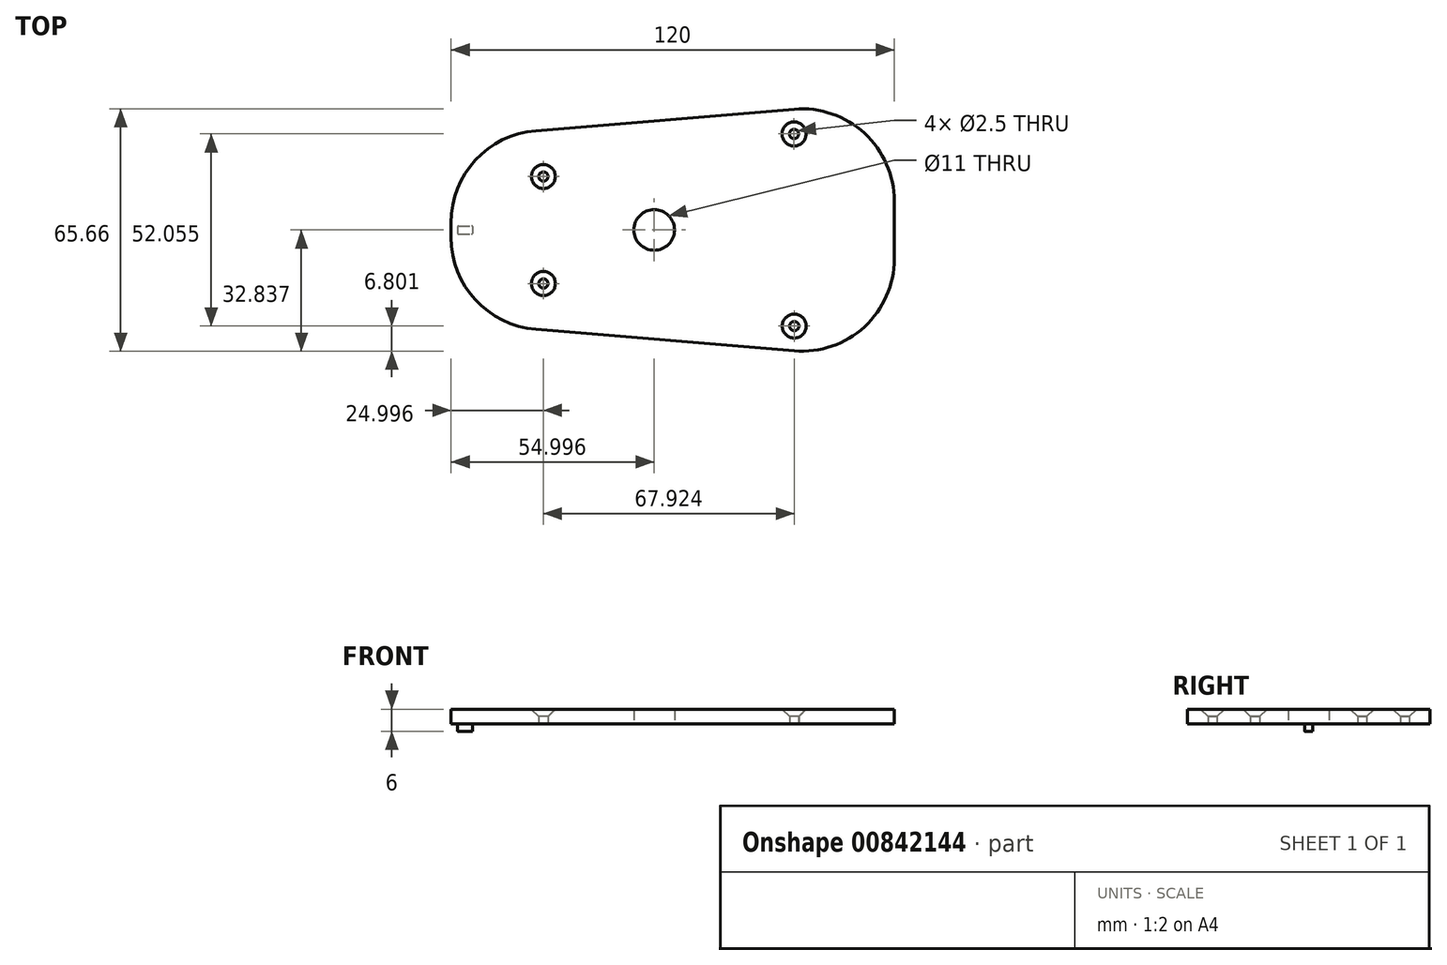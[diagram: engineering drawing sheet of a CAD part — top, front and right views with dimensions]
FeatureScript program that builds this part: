
annotation { "Feature Type Name" : "Feature", "Feature Type Description" : "" }
export const myFeature = defineFeature(function(context is Context, id is Id, definition is map)
    precondition{}
    {
        {
            var Q0;
            Q0=qCreatedBy(makeId("Top.planeOp"),FACE);
            var sketch = newSketch(context, id + "F0", { "sketchPlane" : qUnion([Q0])});
            skArc(sketch, "E0.0.0", {"start": v(-46.03, 5.44) * mm, "mid": v(-48.71, 1) * mm, "end": v(-53.63, -0.65) * mm});
            skLineSegment(sketch, "E0.0.1", {"start": v(-53.63, -0.65) * mm, "end": v(-59.43, -0.65) * mm});
            skLineSegment(sketch, "E0.0.2", {"start": v(-59.43, -0.65) * mm, "end": v(-59.43, -1.35) * mm});
            skArc(sketch, "E0.0.3", {"start": v(-59.43, -1.35) * mm, "mid": v(-52.83, -18.28) * mm, "end": v(-36.5, -26.26) * mm});
            skLineSegment(sketch, "E0.0.4", {"start": v(-36.5, -26.26) * mm, "end": v(33.5, -32.1) * mm});
            skArc(sketch, "E0.0.5", {"start": v(33.5, -32.1) * mm, "mid": v(52.5, -25.58) * mm, "end": v(60.57, -7.18) * mm});
            skLineSegment(sketch, "E0.0.6", {"start": v(60.57, -7.18) * mm, "end": v(60.57, 8.48) * mm});
            skArc(sketch, "E0.0.7", {"start": v(60.57, 8.48) * mm, "mid": v(52.5, 26.88) * mm, "end": v(33.5, 33.4) * mm});
            skLineSegment(sketch, "E0.0.8", {"start": v(33.5, 33.4) * mm, "end": v(-36.5, 27.56) * mm});
            skArc(sketch, "E0.0.9", {"start": v(-36.5, 27.56) * mm, "mid": v(-52.83, 19.57) * mm, "end": v(-59.43, 2.64) * mm});
            skLineSegment(sketch, "E0.0.10", {"start": v(-59.43, 2.64) * mm, "end": v(-59.43, 1.95) * mm});
            skLineSegment(sketch, "E0.0.11", {"start": v(-59.43, 1.95) * mm, "end": v(-53.63, 1.95) * mm});
            skArc(sketch, "E0.0.12", {"start": v(-53.63, 1.95) * mm, "mid": v(-50.35, 2.85) * mm, "end": v(-48.4, 5.63) * mm});
            skArc(sketch, "E0.0.13", {"start": v(-48.4, 5.63) * mm, "mid": v(-40.83, 12.6) * mm, "end": v(-33.43, 5.44) * mm});
            skArc(sketch, "E0.0.14", {"start": v(-33.43, 5.44) * mm, "mid": v(-31.53, 2.84) * mm, "end": v(-28.43, 1.95) * mm});
            skLineSegment(sketch, "E0.0.15", {"start": v(-28.43, 1.95) * mm, "end": v(-15.43, 1.95) * mm});
            skLineSegment(sketch, "E0.0.16", {"start": v(-15.43, 1.95) * mm, "end": v(-15.43, 15.25) * mm});
            skLineSegment(sketch, "E0.0.17", {"start": v(-15.43, 15.25) * mm, "end": v(-4.93, 15.25) * mm});
            skLineSegment(sketch, "E0.0.18", {"start": v(-4.93, 15.25) * mm, "end": v(-4.93, 17.18) * mm});
            skArc(sketch, "E0.0.19", {"start": v(-4.93, 17.18) * mm, "mid": v(-0.83, 21.28) * mm, "end": v(3.27, 17.18) * mm});
            skLineSegment(sketch, "E0.0.20", {"start": v(3.27, 17.18) * mm, "end": v(3.27, 15.25) * mm});
            skLineSegment(sketch, "E0.0.21", {"start": v(3.27, 15.25) * mm, "end": v(29.22, 15.25) * mm});
            skLineSegment(sketch, "E0.0.22", {"start": v(29.22, 15.25) * mm, "end": v(29.22, 17.18) * mm});
            skArc(sketch, "E0.0.23", {"start": v(29.22, 17.18) * mm, "mid": v(33.32, 21.28) * mm, "end": v(37.42, 17.18) * mm});
            skLineSegment(sketch, "E0.0.24", {"start": v(37.42, 17.18) * mm, "end": v(37.42, 15.25) * mm});
            skLineSegment(sketch, "E0.0.25", {"start": v(37.42, 15.25) * mm, "end": v(47.92, 15.25) * mm});
            skLineSegment(sketch, "E0.0.26", {"start": v(47.92, 15.25) * mm, "end": v(47.92, -13.95) * mm});
            skLineSegment(sketch, "E0.0.27", {"start": v(47.92, -13.95) * mm, "end": v(37.42, -13.95) * mm});
            skLineSegment(sketch, "E0.0.28", {"start": v(37.42, -13.95) * mm, "end": v(37.42, -15.88) * mm});
            skArc(sketch, "E0.0.29", {"start": v(37.42, -15.88) * mm, "mid": v(33.32, -19.98) * mm, "end": v(29.22, -15.88) * mm});
            skLineSegment(sketch, "E0.0.30", {"start": v(29.22, -15.88) * mm, "end": v(29.22, -13.95) * mm});
            skLineSegment(sketch, "E0.0.31", {"start": v(29.22, -13.95) * mm, "end": v(3.27, -13.95) * mm});
            skLineSegment(sketch, "E0.0.32", {"start": v(3.27, -13.95) * mm, "end": v(3.27, -15.88) * mm});
            skArc(sketch, "E0.0.33", {"start": v(3.27, -15.88) * mm, "mid": v(-0.83, -19.98) * mm, "end": v(-4.93, -15.88) * mm});
            skLineSegment(sketch, "E0.0.34", {"start": v(-4.93, -15.88) * mm, "end": v(-4.93, -13.95) * mm});
            skLineSegment(sketch, "E0.0.35", {"start": v(-4.93, -13.95) * mm, "end": v(-15.43, -13.95) * mm});
            skLineSegment(sketch, "E0.0.36", {"start": v(-15.43, -13.95) * mm, "end": v(-15.43, -0.65) * mm});
            skLineSegment(sketch, "E0.0.37", {"start": v(-15.43, -0.65) * mm, "end": v(-28.43, -0.65) * mm});
            skArc(sketch, "E0.0.38", {"start": v(-28.43, -0.65) * mm, "mid": v(-33.36, 1) * mm, "end": v(-36.03, 5.44) * mm});
            skArc(sketch, "E0.0.39", {"start": v(-36.03, 5.44) * mm, "mid": v(-41.03, 10.44) * mm, "end": v(-46.03, 5.44) * mm});
            skCircle(sketch, "E1.0", {"center": v(-34.43, 15.14) * mm, "radius": 1.25 * mm});
            skPoint(sketch, "E2.0", {"position": v(-34.43, -13.85) * mm});
            skCircle(sketch, "E3.0", {"center": v(-34.43, -13.85) * mm, "radius": 1.25 * mm});
            skCircle(sketch, "E4.0", {"center": v(33.5, -25.38) * mm, "radius": 1.25 * mm});
            skCircle(sketch, "E5.0", {"center": v(33.43, 26.68) * mm, "radius": 1.25 * mm});
            skCircle(sketch, "E6", {"center": v(-4.43, 0.66) * mm, "radius": 5.5 * mm});
            skLineSegment(sketch, "E7", {"start": v(-53.63, 1.95) * mm, "end": v(-53.63, -0.65) * mm});
            skLineSegment(sketch, "E8", {"start": v(-57.63, 0.65) * mm, "end": v(-57.63, -0.65) * mm});
            skLineSegment(sketch, "E9", {"start": v(-57.63, -0.65) * mm, "end": v(-57.63, 1.95) * mm});
            skLineSegment(sketch, "E10", {"start": v(-59.43, 1.95) * mm, "end": v(-59.43, -0.65) * mm});
            skSolve(sketch);
        }
        {
            var Q0;
            Q0=makeQuery(id+"F0.imprint","IMPRINT",FACE,{"disambiguationData":[TD([[makeQuery(id+"F0.imprint","IMPRINT",EDGE,{"derivedFrom":sQuery(id+"F0.wireOp",EDGE,"f2d0978f-a5e2-4eee-89b1-d31b48b31204.0.0")}),1.0]])]});
            var Q1;
            Q1=makeQuery(id+"F0.imprint","IMPRINT",FACE,{"disambiguationData":[TD([[makeQuery(id+"F0.imprint","IMPRINT",EDGE,{"derivedFrom":sQuery(id+"F0.wireOp",EDGE,"ac3f7785-ddd1-404e-9a58-e7037b63adee.0")}),-1.0]])]});
            var Q2;
            {var subQ9=sQuery(id+"F0.wireOp",EDGE,"E0.0.0");Q2=makeQuery(id+"F0.imprint","IMPRINT",FACE,{"disambiguationData":[TD([[makeQuery(id+"F0.imprint","IMPRINT",EDGE,{"derivedFrom":subQ9}),1.0]])]});}
            var Q3;
            Q3=makeQuery(id+"F0.imprint","IMPRINT",FACE,{"disambiguationData":[TD([[makeQuery(id+"F0.imprint","IMPRINT",EDGE,{"derivedFrom":sQuery(id+"F0.wireOp",EDGE,"E0.0.0")}),-1.0]])]});
            var Q4;
            {var subQ6=sQuery(id+"F0.wireOp",EDGE,"E10");Q4=makeQuery(id+"F0.imprint","IMPRINT",FACE,{"disambiguationData":[TD([[makeQuery(id+"F0.imprint","IMPRINT",EDGE,{"derivedFrom":subQ6}),1.0]])]});}
            var Q5;
            {var subQ0=sQuery(id+"F0.wireOp",EDGE,"E7");Q5=makeQuery(id+"F0.imprint","IMPRINT",FACE,{"disambiguationData":[TD([[makeQuery(id+"F0.imprint","IMPRINT",EDGE,{"derivedFrom":subQ0}),-1.0]])]});}
            extrude(context, id + "F1", {"entities" : qUnion([Q0, Q1, Q2, Q3, Q4, Q5]), "depth" : 4 * mm, "offsetDistance" : 25 * mm});
        }
        {
            var Q0;
            Q0=makeQuery(id+"F1.opExtrude","CAP_FACE",FACE,{"disambiguationData":[OSD([sQuery(id+"F0.wireOp",EDGE,"E0.0.2"),sQuery(id+"F0.wireOp",EDGE,"E0.0.3"),sQuery(id+"F0.wireOp",EDGE,"E0.0.4"),sQuery(id+"F0.wireOp",EDGE,"E0.0.5"),sQuery(id+"F0.wireOp",EDGE,"E0.0.6"),sQuery(id+"F0.wireOp",EDGE,"E0.0.7"),sQuery(id+"F0.wireOp",EDGE,"E0.0.8"),sQuery(id+"F0.wireOp",EDGE,"E0.0.9"),sQuery(id+"F0.wireOp",EDGE,"E0.0.10"),sQuery(id+"F0.wireOp",EDGE,"E1.0"),sQuery(id+"F0.wireOp",EDGE,"E3.0"),sQuery(id+"F0.wireOp",EDGE,"E4.0"),sQuery(id+"F0.wireOp",EDGE,"E5.0"),sQuery(id+"F0.wireOp",EDGE,"E6"),sQuery(id+"F0.wireOp",EDGE,"E10")])],"isStart":true});
            var sketch = newSketch(context, id + "F2", { "sketchPlane" : qUnion([Q0])});
            skArc(sketch, "E11.0", {"start": v(-46.03, -5.44) * mm, "mid": v(-48.71, -1) * mm, "end": v(-53.63, 0.65) * mm});
            skLineSegment(sketch, "E11.1", {"start": v(-53.63, 0.65) * mm, "end": v(-59.43, 0.65) * mm});
            skLineSegment(sketch, "E11.2", {"start": v(-59.43, 0.65) * mm, "end": v(-59.43, 1.35) * mm});
            skArc(sketch, "E11.3", {"start": v(-59.43, 1.35) * mm, "mid": v(-52.83, 18.28) * mm, "end": v(-36.5, 26.26) * mm});
            skLineSegment(sketch, "E11.4", {"start": v(-36.5, 26.26) * mm, "end": v(33.5, 32.1) * mm});
            skArc(sketch, "E11.5", {"start": v(33.5, 32.1) * mm, "mid": v(52.5, 25.58) * mm, "end": v(60.57, 7.18) * mm});
            skLineSegment(sketch, "E11.6", {"start": v(60.57, 7.18) * mm, "end": v(60.57, -8.48) * mm});
            skArc(sketch, "E11.7", {"start": v(60.57, -8.48) * mm, "mid": v(52.5, -26.88) * mm, "end": v(33.5, -33.4) * mm});
            skLineSegment(sketch, "E11.8", {"start": v(33.5, -33.4) * mm, "end": v(-36.5, -27.56) * mm});
            skArc(sketch, "E11.9", {"start": v(-36.5, -27.56) * mm, "mid": v(-52.83, -19.57) * mm, "end": v(-59.43, -2.64) * mm});
            skLineSegment(sketch, "E11.10", {"start": v(-59.43, -2.64) * mm, "end": v(-59.43, -1.95) * mm});
            skLineSegment(sketch, "E11.11", {"start": v(-59.43, -1.95) * mm, "end": v(-53.63, -1.95) * mm});
            skArc(sketch, "E11.12", {"start": v(-53.63, -1.95) * mm, "mid": v(-50.35, -2.85) * mm, "end": v(-48.4, -5.63) * mm});
            skArc(sketch, "E11.13", {"start": v(-48.4, -5.63) * mm, "mid": v(-40.83, -12.6) * mm, "end": v(-33.43, -5.44) * mm});
            skArc(sketch, "E11.14", {"start": v(-33.43, -5.44) * mm, "mid": v(-31.53, -2.84) * mm, "end": v(-28.43, -1.95) * mm});
            skLineSegment(sketch, "E11.15", {"start": v(-28.43, -1.95) * mm, "end": v(-15.43, -1.95) * mm});
            skLineSegment(sketch, "E11.16", {"start": v(-15.43, -1.95) * mm, "end": v(-15.43, -15.25) * mm});
            skLineSegment(sketch, "E11.17", {"start": v(-15.43, -15.25) * mm, "end": v(-4.93, -15.25) * mm});
            skLineSegment(sketch, "E11.18", {"start": v(-4.93, -15.25) * mm, "end": v(-4.93, -17.18) * mm});
            skArc(sketch, "E11.19", {"start": v(-4.93, -17.18) * mm, "mid": v(-0.83, -21.28) * mm, "end": v(3.27, -17.18) * mm});
            skLineSegment(sketch, "E11.20", {"start": v(3.27, -17.18) * mm, "end": v(3.27, -15.25) * mm});
            skLineSegment(sketch, "E11.21", {"start": v(3.27, -15.25) * mm, "end": v(29.22, -15.25) * mm});
            skLineSegment(sketch, "E11.22", {"start": v(29.22, -15.25) * mm, "end": v(29.22, -17.18) * mm});
            skArc(sketch, "E11.23", {"start": v(29.22, -17.18) * mm, "mid": v(33.32, -21.28) * mm, "end": v(37.42, -17.18) * mm});
            skLineSegment(sketch, "E11.24", {"start": v(37.42, -17.18) * mm, "end": v(37.42, -15.25) * mm});
            skLineSegment(sketch, "E11.25", {"start": v(37.42, -15.25) * mm, "end": v(47.92, -15.25) * mm});
            skLineSegment(sketch, "E11.26", {"start": v(47.92, -15.25) * mm, "end": v(47.92, 13.95) * mm});
            skLineSegment(sketch, "E11.27", {"start": v(47.92, 13.95) * mm, "end": v(37.42, 13.95) * mm});
            skLineSegment(sketch, "E11.28", {"start": v(37.42, 13.95) * mm, "end": v(37.42, 15.88) * mm});
            skArc(sketch, "E11.29", {"start": v(37.42, 15.88) * mm, "mid": v(33.32, 19.98) * mm, "end": v(29.22, 15.88) * mm});
            skLineSegment(sketch, "E11.30", {"start": v(29.22, 15.88) * mm, "end": v(29.22, 13.95) * mm});
            skLineSegment(sketch, "E11.31", {"start": v(29.22, 13.95) * mm, "end": v(3.27, 13.95) * mm});
            skLineSegment(sketch, "E11.32", {"start": v(3.27, 13.95) * mm, "end": v(3.27, 15.88) * mm});
            skArc(sketch, "E11.33", {"start": v(3.27, 15.88) * mm, "mid": v(-0.83, 19.98) * mm, "end": v(-4.93, 15.88) * mm});
            skLineSegment(sketch, "E11.34", {"start": v(-4.93, 15.88) * mm, "end": v(-4.93, 13.95) * mm});
            skLineSegment(sketch, "E11.35", {"start": v(-4.93, 13.95) * mm, "end": v(-15.43, 13.95) * mm});
            skLineSegment(sketch, "E11.36", {"start": v(-15.43, 13.95) * mm, "end": v(-15.43, 0.65) * mm});
            skLineSegment(sketch, "E11.37", {"start": v(-15.43, 0.65) * mm, "end": v(-28.43, 0.65) * mm});
            skArc(sketch, "E11.38", {"start": v(-28.43, 0.65) * mm, "mid": v(-33.36, -1) * mm, "end": v(-36.03, -5.44) * mm});
            skArc(sketch, "E11.39", {"start": v(-36.03, -5.44) * mm, "mid": v(-41.03, -10.44) * mm, "end": v(-46.03, -5.44) * mm});
            skCircle(sketch, "E11.40", {"center": v(-34.43, -15.14) * mm, "radius": 1.25 * mm});
            skPoint(sketch, "E11.41", {"position": v(-34.43, 13.85) * mm});
            skCircle(sketch, "E11.42", {"center": v(-34.43, 13.85) * mm, "radius": 1.25 * mm});
            skCircle(sketch, "E11.43", {"center": v(33.5, 25.38) * mm, "radius": 1.25 * mm});
            skCircle(sketch, "E11.44", {"center": v(33.43, -26.68) * mm, "radius": 1.25 * mm});
            skCircle(sketch, "E11.45", {"center": v(-4.43, -0.66) * mm, "radius": 5.5 * mm});
            skLineSegment(sketch, "E11.46", {"start": v(-53.63, -1.55) * mm, "end": v(-53.63, 0.25) * mm});
            skLineSegment(sketch, "E11.47", {"start": v(-57.63, -0.65) * mm, "end": v(-57.63, 0.25) * mm});
            skLineSegment(sketch, "E11.48", {"start": v(-57.63, 0.25) * mm, "end": v(-57.63, -1.55) * mm});
            skLineSegment(sketch, "E11.49", {"start": v(-59.43, -1.95) * mm, "end": v(-59.43, 0.65) * mm});
            skLineSegment(sketch, "E12", {"start": v(-57.43, 0.45) * mm, "end": v(-53.83, 0.45) * mm});
            skLineSegment(sketch, "E13", {"start": v(-57.43, -1.75) * mm, "end": v(-53.83, -1.75) * mm});
            skPoint(sketch, "E14.orphan", {"position": v(-57.63, 0.65) * mm});
            skPoint(sketch, "E15.orphan", {"position": v(-57.63, -1.95) * mm});
            skPoint(sketch, "E16.orphan", {"position": v(-53.63, -1.95) * mm});
            skPoint(sketch, "E17.orphan", {"position": v(-53.63, 0.65) * mm});
            skArc(sketch, "E18", {"start": v(-57.43, 0.45) * mm, "mid": v(-57.58, 0.4) * mm, "end": v(-57.63, 0.25) * mm});
            skArc(sketch, "E19", {"start": v(-53.63, 0.25) * mm, "mid": v(-53.7, 0.4) * mm, "end": v(-53.83, 0.45) * mm});
            skArc(sketch, "E20.MirrorCS", {"start": v(-57.43, -1.75) * mm, "mid": v(-57.58, -1.69) * mm, "end": v(-57.63, -1.55) * mm});
            skArc(sketch, "E21.MirrorCS", {"start": v(-53.63, -1.55) * mm, "mid": v(-53.7, -1.69) * mm, "end": v(-53.83, -1.75) * mm});
            skPoint(sketch, "E22.orphan", {"position": v(-53.63, -1.75) * mm});
            skPoint(sketch, "E23.trimOffspring.end.orphan", {"position": v(-53.63, -0.65) * mm});
            skPoint(sketch, "E24.orphan", {"position": v(-53.63, 0.45) * mm});
            skSolve(sketch);
        }
        {
            var Q0;
            {var subQ0=sQuery(id+"F2.wireOp",EDGE,"E11.46");Q0=makeQuery(id+"F2.imprint","IMPRINT",FACE,{"disambiguationData":[TD([[makeQuery(id+"F2.imprint","IMPRINT",EDGE,{"derivedFrom":subQ0}),1.0]])]});}
            extrude(context, id + "F3", {"entities" : qUnion([Q0]), "operationType" : NewBodyOperationType.ADD, "depth" : 2 * mm, "offsetDistance" : 25 * mm});
        }
        {
            var Q0;
            Q0=makeQuery(id+"F1.opExtrude","CAP_EDGE",EDGE,{"disambiguationData":[OSD([sQuery(id+"F0.wireOp",EDGE,"E1.0")])],"isStart":false});
            var Q1;
            Q1=makeQuery(id+"F1.opExtrude","CAP_EDGE",EDGE,{"disambiguationData":[OSD([sQuery(id+"F0.wireOp",EDGE,"E3.0")])],"isStart":false});
            var Q2;
            Q2=makeQuery(id+"F1.opExtrude","CAP_EDGE",EDGE,{"disambiguationData":[OSD([sQuery(id+"F0.wireOp",EDGE,"E5.0")])],"isStart":false});
            var Q3;
            Q3=makeQuery(id+"F1.opExtrude","CAP_EDGE",EDGE,{"disambiguationData":[OSD([sQuery(id+"F0.wireOp",EDGE,"E4.0")])],"isStart":false});
            chamfer(context, id + "F4", {"entities" : qUnion([Q0, Q1, Q2, Q3]), "width" : 2 * mm, "tangentPropagation" : true});
        }
    });
